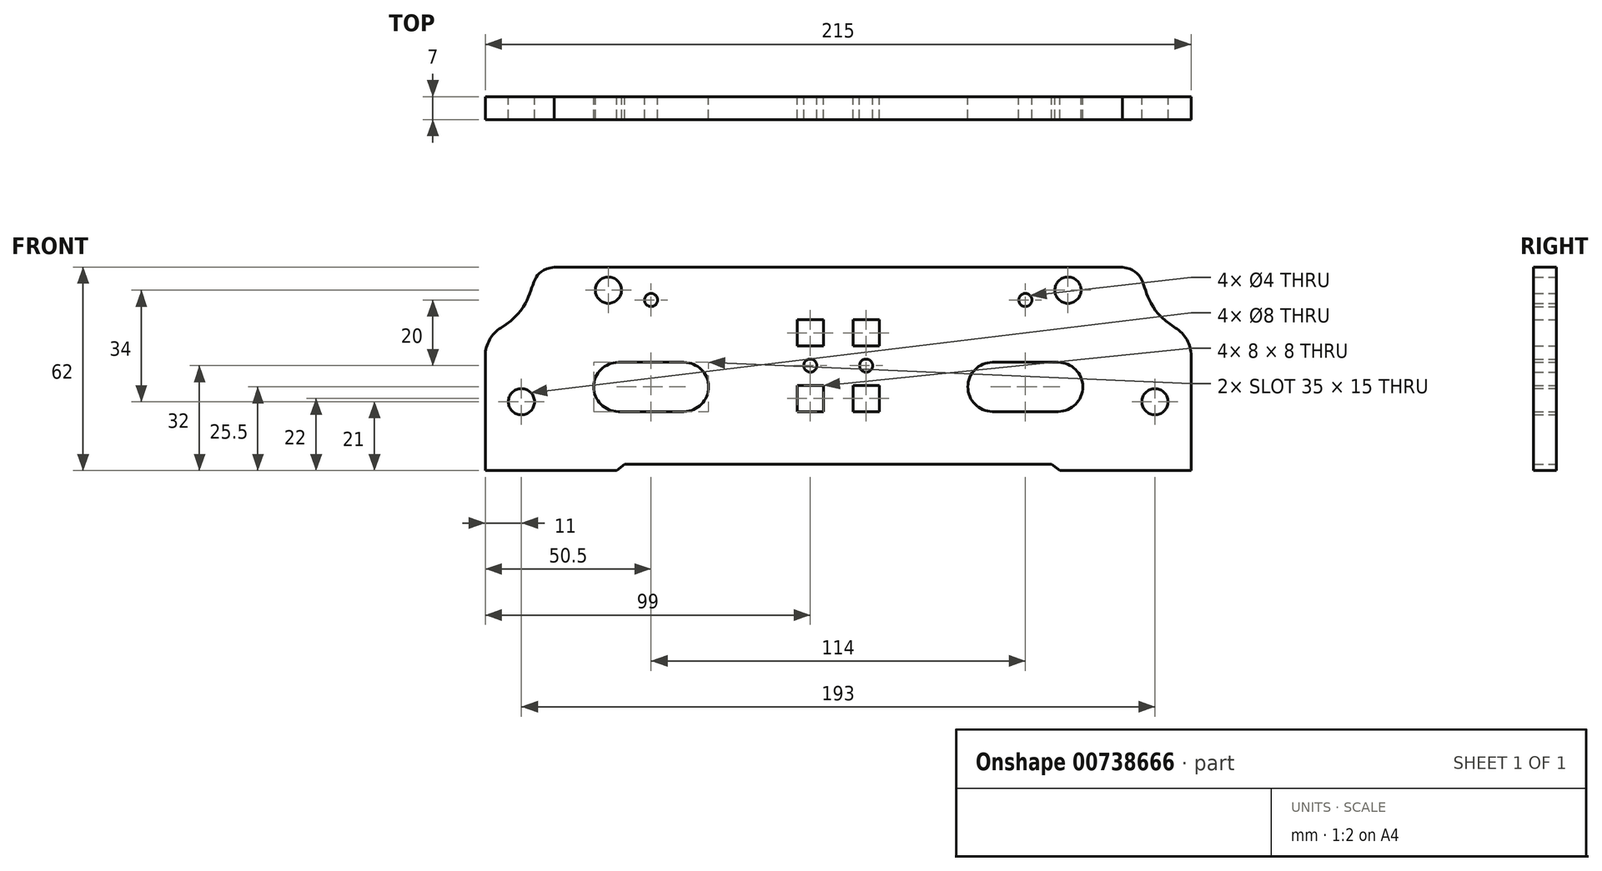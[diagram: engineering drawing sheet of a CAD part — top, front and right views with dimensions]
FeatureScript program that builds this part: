
annotation { "Feature Type Name" : "Feature", "Feature Type Description" : "" }
export const myFeature = defineFeature(function(context is Context, id is Id, definition is map)
    precondition{}
    {
        {
            var Q0;
            Q0=qCreatedBy(makeId("Front.planeOp"),FACE);
            var sketch = newSketch(context, id + "F0", { "sketchPlane" : qUnion([Q0])});
            skLineSegment(sketch, "E0", {"start": v(0, 0) * mm, "end": v(65, 0) * mm});
            skLineSegment(sketch, "E1", {"start": v(65, 0) * mm, "end": v(67.5, -2) * mm});
            skLineSegment(sketch, "E2", {"start": v(67.5, -2) * mm, "end": v(107.5, -2) * mm});
            skLineSegment(sketch, "E3", {"start": v(107.5, -2) * mm, "end": v(107.5, 33) * mm});
            skLineSegment(sketch, "E4", {"start": v(86.54, 60) * mm, "end": v(0, 60) * mm});
            skLineSegment(sketch, "E5", {"start": v(0, 60) * mm, "end": v(0, 0) * mm, "construction": true});
            skFitSpline(sketch, "E6", {"points": [v(86.54, 60) * mm, v(107.5, 39.07) * mm], "startDerivative": vector(33.25, -4.14) * mm, "endDerivative": vector(58.4, -25.43) * mm});
            skCircle(sketch, "E7", {"center": v(8.5, 30) * mm, "radius": 2 * mm});
            skLineSegment(sketch, "E8", {"start": v(6.5, 30) * mm, "end": v(10.5, 30) * mm, "construction": true});
            skLineSegment(sketch, "E9", {"start": v(8.5, 0) * mm, "end": v(8.5, 60) * mm, "construction": true});
            skLineSegment(sketch, "E10.bottom", {"start": v(12.5, 44) * mm, "end": v(4.5, 44) * mm});
            skLineSegment(sketch, "E10.top", {"start": v(12.5, 36) * mm, "end": v(4.5, 36) * mm});
            skLineSegment(sketch, "E10.left", {"start": v(12.5, 44) * mm, "end": v(12.5, 36) * mm});
            skLineSegment(sketch, "E10.right", {"start": v(4.5, 44) * mm, "end": v(4.5, 36) * mm});
            skPoint(sketch, "E10.middle", {"position": v(8.5, 40) * mm});
            skLineSegment(sketch, "E11.MirrorCS", {"start": v(4.5, 16) * mm, "end": v(4.5, 24) * mm});
            skLineSegment(sketch, "E12.MirrorCS", {"start": v(12.5, 16) * mm, "end": v(4.5, 16) * mm});
            skLineSegment(sketch, "E13.MirrorCS", {"start": v(12.5, 16) * mm, "end": v(12.5, 24) * mm});
            skLineSegment(sketch, "E14.MirrorCS", {"start": v(12.5, 24) * mm, "end": v(4.5, 24) * mm});
            skArc(sketch, "E15", {"start": v(47, 31) * mm, "mid": v(39.5, 23.5) * mm, "end": v(47, 16) * mm});
            skArc(sketch, "E16", {"start": v(67, 16) * mm, "mid": v(74.5, 23.5) * mm, "end": v(67, 31) * mm});
            skLineSegment(sketch, "E17", {"start": v(47, 31) * mm, "end": v(67, 31) * mm});
            skLineSegment(sketch, "E18", {"start": v(47, 16) * mm, "end": v(67, 16) * mm});
            skCircle(sketch, "E19", {"center": v(57, 50) * mm, "radius": 2 * mm});
            skCircle(sketch, "E20", {"center": v(70, 53) * mm, "radius": 4 * mm});
            skLineSegment(sketch, "E21", {"start": v(57, 31) * mm, "end": v(57, 60) * mm, "construction": true});
            skCircle(sketch, "E22", {"center": v(96.5, 19) * mm, "radius": 4 * mm});
            skArc(sketch, "E23.filletArc", {"start": v(107.5, 33) * mm, "mid": v(106.23, 37.89) * mm, "end": v(102.73, 41.53) * mm});
            skLineSegment(sketch, "E24.MirrorCS", {"start": v(-65, 0) * mm, "end": v(-67.5, -2) * mm});
            skArc(sketch, "E25.MirrorCS", {"start": v(-107.5, 33) * mm, "mid": v(-106.23, 37.89) * mm, "end": v(-102.73, 41.53) * mm});
            skCircle(sketch, "E26.MirrorC", {"center": v(-57, 50) * mm, "radius": 2 * mm});
            skCircle(sketch, "E27.MirrorC", {"center": v(-8.5, 30) * mm, "radius": 2 * mm});
            skLineSegment(sketch, "E28.MirrorCS", {"start": v(-6.5, 30) * mm, "end": v(-10.5, 30) * mm, "construction": true});
            skLineSegment(sketch, "E29.MirrorCS", {"start": v(-12.5, 16) * mm, "end": v(-12.5, 24) * mm});
            skPoint(sketch, "E30.MirrorP", {"position": v(-107.5, 39.07) * mm});
            skArc(sketch, "E31.MirrorCS", {"start": v(-47, 31) * mm, "mid": v(-39.5, 23.5) * mm, "end": v(-47, 16) * mm});
            skPoint(sketch, "E32.MirrorP", {"position": v(-8.5, 40) * mm});
            skLineSegment(sketch, "E33.MirrorCS", {"start": v(-47, 31) * mm, "end": v(-67, 31) * mm});
            skLineSegment(sketch, "E34.MirrorCS", {"start": v(-47, 16) * mm, "end": v(-67, 16) * mm});
            skCircle(sketch, "E35.MirrorC", {"center": v(-70, 53) * mm, "radius": 4 * mm});
            skCircle(sketch, "E36.MirrorC", {"center": v(-96.5, 19) * mm, "radius": 4 * mm});
            skLineSegment(sketch, "E37.MirrorCS", {"start": v(-12.5, 44) * mm, "end": v(-12.5, 36) * mm});
            skArc(sketch, "E38.MirrorCS", {"start": v(-67, 16) * mm, "mid": v(-74.5, 23.5) * mm, "end": v(-67, 31) * mm});
            skLineSegment(sketch, "E39.MirrorCS", {"start": v(-12.5, 36) * mm, "end": v(-4.5, 36) * mm});
            skFitSpline(sketch, "E40.MirrorCS", {"points": [v(-86.54, 60) * mm, v(-107.5, 39.07) * mm], "startDerivative": vector(-33.25, -4.14) * mm, "endDerivative": vector(-58.4, -25.43) * mm});
            skLineSegment(sketch, "E41.MirrorCS", {"start": v(-4.5, 16) * mm, "end": v(-4.5, 24) * mm});
            skLineSegment(sketch, "E42.MirrorCS", {"start": v(-12.5, 44) * mm, "end": v(-4.5, 44) * mm});
            skLineSegment(sketch, "E43.MirrorCS", {"start": v(-86.54, 60) * mm, "end": v(0, 60) * mm});
            skLineSegment(sketch, "E44.MirrorCS", {"start": v(0, 0) * mm, "end": v(-65, 0) * mm});
            skLineSegment(sketch, "E45.MirrorCS", {"start": v(-4.5, 44) * mm, "end": v(-4.5, 36) * mm});
            skLineSegment(sketch, "E46.MirrorCS", {"start": v(-8.5, 0) * mm, "end": v(-8.5, 60) * mm, "construction": true});
            skLineSegment(sketch, "E47.MirrorCS", {"start": v(-57, 31) * mm, "end": v(-57, 60) * mm, "construction": true});
            skLineSegment(sketch, "E48.MirrorCS", {"start": v(-67.5, -2) * mm, "end": v(-107.5, -2) * mm});
            skLineSegment(sketch, "E49.MirrorCS", {"start": v(-12.5, 24) * mm, "end": v(-4.5, 24) * mm});
            skLineSegment(sketch, "E50.MirrorCS", {"start": v(-12.5, 16) * mm, "end": v(-4.5, 16) * mm});
            skLineSegment(sketch, "E51.MirrorCS", {"start": v(-107.5, -2) * mm, "end": v(-107.5, 33) * mm});
            skSolve(sketch);
        }
        {
            var Q0;
            Q0 = qSketchRegion(id + "F0", true);
            extrude(context, id + "F1", {"entities" : qUnion([Q0]), "depth" : 7 * mm, "offsetDistance" : 25 * mm});
        }
    });
